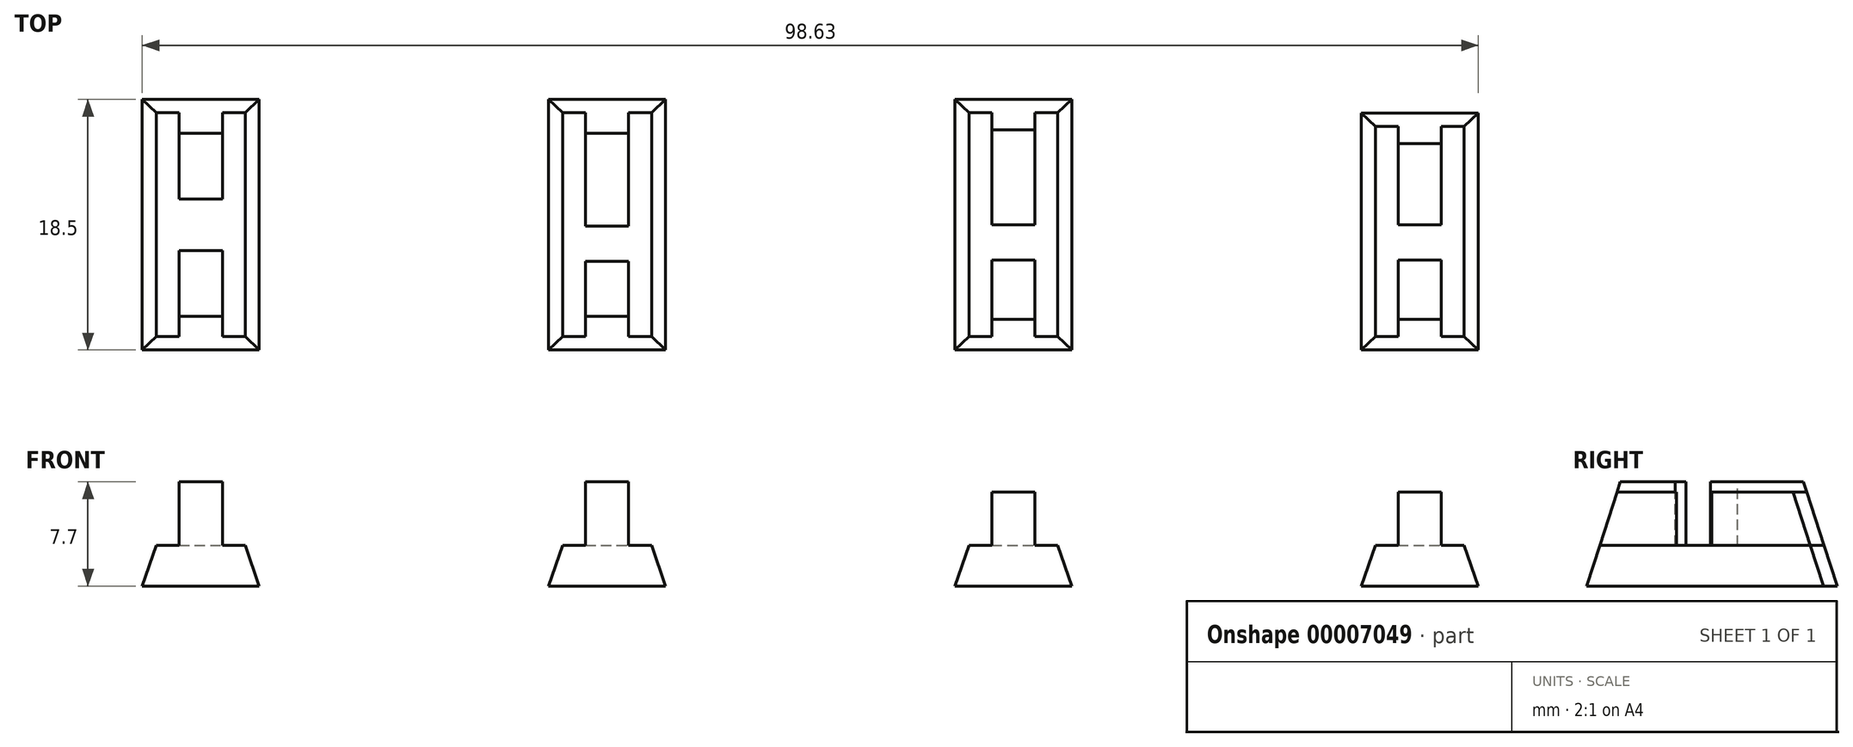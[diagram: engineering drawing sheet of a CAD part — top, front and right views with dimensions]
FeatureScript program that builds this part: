
annotation { "Feature Type Name" : "Feature", "Feature Type Description" : "" }
export const myFeature = defineFeature(function(context is Context, id is Id, definition is map)
    precondition{}
    {
        {
            var Q0;
            Q0=qCreatedBy(makeId("Front.planeOp"),FACE);
            var sketch = newSketch(context, id + "F0", { "sketchPlane" : qUnion([Q0])});
            skLineSegment(sketch, "E0", {"start": v(-34.23, 16.07) * mm, "end": v(-34.23, 12.67) * mm, "construction": true});
            skLineSegment(sketch, "E1", {"start": v(-34.23, 14.54) * mm, "end": v(-38.54, 14.54) * mm});
            skLineSegment(sketch, "E2", {"start": v(-38.54, 14.54) * mm, "end": v(-43.22, 14.54) * mm, "construction": true});
            skLineSegment(sketch, "E3", {"start": v(-43.22, 14.54) * mm, "end": v(-43.22, 17.54) * mm, "construction": true});
            skLineSegment(sketch, "E4", {"start": v(-43.22, 17.54) * mm, "end": v(-31.38, 17.54) * mm, "construction": true});
            skLineSegment(sketch, "E5", {"start": v(-37.5, 16.07) * mm, "end": v(-37.5, 22.5) * mm, "construction": true});
            skLineSegment(sketch, "E6", {"start": v(-38.54, 14.54) * mm, "end": v(-37.5, 17.54) * mm});
            skPoint(sketch, "E6.endSnap0", {"position": v(-37.3, 17.54) * mm});
            skLineSegment(sketch, "E7", {"start": v(-37.5, 17.54) * mm, "end": v(-35.82, 17.54) * mm});
            skLineSegment(sketch, "E8", {"start": v(-35.82, 17.54) * mm, "end": v(-35.82, 22.24) * mm});
            skLineSegment(sketch, "E9", {"start": v(-34.23, 14.54) * mm, "end": v(-34.23, 23.56) * mm, "construction": true});
            skLineSegment(sketch, "E10", {"start": v(-35.82, 22.24) * mm, "end": v(-34.23, 22.24) * mm});
            skLineSegment(sketch, "E11", {"start": v(-34.23, 22.24) * mm, "end": v(-34.23, 14.54) * mm});
            skSolve(sketch);
        }
        {
            var Q0;
            Q0=makeQuery(id+"F0.imprint","IMPRINT",FACE,{"disambiguationData":[TD([[makeQuery(id+"F0.imprint","IMPRINT",EDGE,{"derivedFrom":sQuery(id+"F0.wireOp",EDGE,"E1")}),-1.0]])]});
            extrude(context, id + "F1", {"entities" : qUnion([Q0]), "depth" : 18.5 * mm});
        }
        {
            var Q0;
            Q0=makeQuery(id+"F1.opExtrude","SWEPT_FACE",FACE,{"disambiguationData":[OSD([sQuery(id+"F0.wireOp",EDGE,"E11")])]});
            var sketch = newSketch(context, id + "F2", { "sketchPlane" : qUnion([Q0])});
            skLineSegment(sketch, "E12", {"start": v(-9.25, 22.24) * mm, "end": v(-9.25, 26.61) * mm, "construction": true});
            skCircle(sketch, "E13", {"center": v(-9.25, 26.61) * mm, "radius": 1.9 * mm, "construction": true});
            skLineSegment(sketch, "E14", {"start": v(-18.5, 14.54) * mm, "end": v(-16, 22.24) * mm});
            skLineSegment(sketch, "E15.MirrorCS", {"start": v(0, 14.54) * mm, "end": v(-2.5, 22.24) * mm});
            skLineSegment(sketch, "E16", {"start": v(-9.25, 26.61) * mm, "end": v(-11.15, 26.61) * mm, "construction": true});
            skLineSegment(sketch, "E17", {"start": v(-11.15, 26.61) * mm, "end": v(-11.15, 12.36) * mm, "construction": true});
            skLineSegment(sketch, "E18", {"start": v(-11.15, 22.24) * mm, "end": v(-11.15, 17.54) * mm});
            skLineSegment(sketch, "E19.MirrorCS", {"start": v(-7.35, 22.24) * mm, "end": v(-7.35, 17.54) * mm});
            skLineSegment(sketch, "E20", {"start": v(-11.15, 17.54) * mm, "end": v(-7.35, 17.54) * mm});
            skSolve(sketch);
        }
        {
            var Q0;
            {var subQ3=sQuery(id+"F2.wireOp",EDGE,"E14");Q0=makeQuery(id+"F2.imprint","IMPRINT",FACE,{"disambiguationData":[TD([[makeQuery(id+"F2.imprint","IMPRINT",EDGE,{"derivedFrom":subQ3}),1.0]])]});}
            var Q1;
            {var subQ3=sQuery(id+"F2.wireOp",EDGE,"E15.MirrorCS");Q1=makeQuery(id+"F2.imprint","IMPRINT",FACE,{"disambiguationData":[TD([[makeQuery(id+"F2.imprint","IMPRINT",EDGE,{"derivedFrom":subQ3}),-1.0]])]});}
            var Q2;
            {var subQ2=sQuery(id+"F2.wireOp",EDGE,"E18");Q2=makeQuery(id+"F2.imprint","IMPRINT",FACE,{"disambiguationData":[TD([[makeQuery(id+"F2.imprint","IMPRINT",EDGE,{"derivedFrom":subQ2}),1.0]])]});}
            extrude(context, id + "F3", {"entities" : qUnion([Q0, Q1, Q2]), "operationType" : NewBodyOperationType.REMOVE, "oppositeDirection" : true, "depth" : 10 * mm});
        }
        {
            var Q0;
            Q0=makeQuery(id+"F1.opExtrude","SWEPT_BODY",BODY,{"disambiguationData":[OSD([sQuery(id+"F0.wireOp",EDGE,"E1"),sQuery(id+"F0.wireOp",EDGE,"E6"),sQuery(id+"F0.wireOp",EDGE,"E7"),sQuery(id+"F0.wireOp",EDGE,"E8"),sQuery(id+"F0.wireOp",EDGE,"E10"),sQuery(id+"F0.wireOp",EDGE,"E11")])]});
            var Q1;
            Q1=makeQuery(id+"F1.opExtrude","SWEPT_FACE",FACE,{"disambiguationData":[OSD([sQuery(id+"F0.wireOp",EDGE,"E11")])]});
            mirror(context, id + "F4", {"operationType" : NewBodyOperationType.ADD, "entities" : qUnion([Q0]), "mirrorPlane" : qUnion([Q1])});
        }
        {
            var Q0;
            Q0=makeQuery(id+"F1.opExtrude","SWEPT_BODY",BODY,{"disambiguationData":[OSD([sQuery(id+"F0.wireOp",EDGE,"E1"),sQuery(id+"F0.wireOp",EDGE,"E6"),sQuery(id+"F0.wireOp",EDGE,"E7"),sQuery(id+"F0.wireOp",EDGE,"E8"),sQuery(id+"F0.wireOp",EDGE,"E10"),sQuery(id+"F0.wireOp",EDGE,"E11")])]});
            transform(context, id + "F5", {"entities" : qUnion([Q0]), "transformType" : TransformType.TRANSLATION_3D, "dx" : 30 * mm, "dy" : 0 * mm, "dz" : 0 * mm, "makeCopy" : true});
        }
        {
            var Q0;
            {var subQ0=makeQuery(id+"F3.boolean.opBoolean","COPY",FACE,{"derivedFrom":makeQuery(id+"F3.opExtrude","SWEPT_FACE",FACE,{"disambiguationData":[OSD([sQuery(id+"F2.wireOp",EDGE,"E19.MirrorCS")])]})});Q0=makeQuery(id+"F5.opPattern","COPY",FACE,{"derivedFrom":makeQuery(id+"F4.boolean.opBoolean","MERGE",FACE,{"derivedFrom":[subQ0,makeQuery(id+"F4.opPattern","COPY",FACE,{"derivedFrom":subQ0,"instanceName":"1"})]}),"instanceName":"1"});}
            extrude(context, id + "F6", {"entities" : qUnion([Q0]), "operationType" : NewBodyOperationType.ADD, "depth" : 2 * mm});
        }
        {
            var Q0;
            {var subQ0=makeQuery(id+"F3.boolean.opBoolean","COPY",FACE,{"derivedFrom":makeQuery(id+"F3.opExtrude","SWEPT_FACE",FACE,{"disambiguationData":[OSD([sQuery(id+"F2.wireOp",EDGE,"E18")])]})});Q0=makeQuery(id+"F5.opPattern","COPY",FACE,{"derivedFrom":makeQuery(id+"F4.boolean.opBoolean","MERGE",FACE,{"derivedFrom":[subQ0,makeQuery(id+"F4.opPattern","COPY",FACE,{"derivedFrom":subQ0,"instanceName":"1"})]}),"instanceName":"1"});}
            extrude(context, id + "F7", {"entities" : qUnion([Q0]), "operationType" : NewBodyOperationType.REMOVE, "oppositeDirection" : true, "depth" : 0.8 * mm});
        }
        {
            var Q0;
            Q0=makeQuery(id+"F5.opPattern","COPY",BODY,{"derivedFrom":makeQuery(id+"F1.opExtrude","SWEPT_BODY",BODY,{"disambiguationData":[OSD([sQuery(id+"F0.wireOp",EDGE,"E1"),sQuery(id+"F0.wireOp",EDGE,"E6"),sQuery(id+"F0.wireOp",EDGE,"E7"),sQuery(id+"F0.wireOp",EDGE,"E8"),sQuery(id+"F0.wireOp",EDGE,"E10"),sQuery(id+"F0.wireOp",EDGE,"E11")])]}),"instanceName":"1"});
            transform(context, id + "F8", {"entities" : qUnion([Q0]), "transformType" : TransformType.TRANSLATION_3D, "dx" : 30 * mm, "dy" : 0 * mm, "dz" : 0 * mm, "makeCopy" : true});
        }
        {
            var Q0;
            Q0=makeQuery(id+"F8.opPattern","COPY",FACE,{"derivedFrom":makeQuery(id+"F6.opExtrude","CAP_FACE",FACE,{"disambiguationData":[OSD([sQuery(id+"F2.wireOp",EDGE,"E19.MirrorCS")])],"isStart":false}),"instanceName":"1"});
            extrude(context, id + "F9", {"entities" : qUnion([Q0]), "operationType" : NewBodyOperationType.REMOVE, "oppositeDirection" : true, "depth" : 0.1 * mm});
        }
        {
            var Q0;
            Q0=makeQuery(id+"F8.opPattern","COPY",FACE,{"derivedFrom":makeQuery(id+"F7.boolean.opBoolean","COPY",FACE,{"derivedFrom":makeQuery(id+"F7.opExtrude","CAP_FACE",FACE,{"disambiguationData":[OSD([sQuery(id+"F2.wireOp",EDGE,"E18")])],"isStart":false})}),"instanceName":"1"});
            extrude(context, id + "F10", {"entities" : qUnion([Q0]), "operationType" : NewBodyOperationType.ADD, "depth" : 0.1 * mm});
        }
        {
            var Q0;
            {var subQ0=sQuery(id+"F0.wireOp",EDGE,"E10");var subQ1=sQuery(id+"F0.wireOp",EDGE,"E11");var subQ2=sQuery(id+"F2.wireOp",EDGE,"E18");var subQ3=makeQuery(id+"F3.boolean.opBoolean","SPLIT",FACE,{"disambiguationData":[TD([makeQuery(id+"F3.opExtrude","SWEPT_FACE",FACE,{"disambiguationData":[OSD([sQuery(id+"F2.wireOp",EDGE,"E14")])]})])],"derivedFrom":makeQuery(id+"F1.opExtrude","SWEPT_FACE",FACE,{"disambiguationData":[OSD([subQ0])]})});Q0=makeQuery(id+"F10.boolean.opBoolean","MERGE",FACE,{"derivedFrom":[makeQuery(id+"F8.opPattern","COPY",FACE,{"derivedFrom":makeQuery(id+"F5.opPattern","COPY",FACE,{"derivedFrom":makeQuery(id+"F4.boolean.opBoolean","MERGE",FACE,{"derivedFrom":[subQ3,makeQuery(id+"F4.opPattern","COPY",FACE,{"derivedFrom":subQ3,"instanceName":"1"})]}),"instanceName":"1"}),"instanceName":"1"}),makeQuery(id+"F10.opExtrude","SWEPT_FACE",FACE,{"disambiguationData":[OSD([subQ0,subQ1,subQ2])]})]});}
            var Q1;
            {var subQ0=sQuery(id+"F0.wireOp",EDGE,"E10");var subQ1=sQuery(id+"F2.wireOp",EDGE,"E19.MirrorCS");var subQ2=sQuery(id+"F0.wireOp",EDGE,"E11");var subQ3=makeQuery(id+"F3.boolean.opBoolean","SPLIT",FACE,{"disambiguationData":[TD([makeQuery(id+"F3.opExtrude","SWEPT_FACE",FACE,{"disambiguationData":[OSD([sQuery(id+"F2.wireOp",EDGE,"E15.MirrorCS")])]})])],"derivedFrom":makeQuery(id+"F1.opExtrude","SWEPT_FACE",FACE,{"disambiguationData":[OSD([subQ0])]})});Q1=makeQuery(id+"F8.opPattern","COPY",FACE,{"derivedFrom":makeQuery(id+"F6.boolean.opBoolean","MERGE",FACE,{"derivedFrom":[makeQuery(id+"F5.opPattern","COPY",FACE,{"derivedFrom":makeQuery(id+"F4.boolean.opBoolean","MERGE",FACE,{"derivedFrom":[subQ3,makeQuery(id+"F4.opPattern","COPY",FACE,{"derivedFrom":subQ3,"instanceName":"1"})]}),"instanceName":"1"}),makeQuery(id+"F6.opExtrude","SWEPT_FACE",FACE,{"disambiguationData":[OSD([subQ0,subQ2,subQ1])]})]}),"instanceName":"1"});}
            extrude(context, id + "F11", {"entities" : qUnion([Q0, Q1]), "operationType" : NewBodyOperationType.REMOVE, "oppositeDirection" : true, "depth" : 0.75 * mm});
        }
        {
            var Q0;
            Q0=makeQuery(id+"F11.boolean.opBoolean","COPY",FACE,{"derivedFrom":makeQuery(id+"F11.opExtrude","SWEPT_FACE",FACE,{"disambiguationData":[OSD([sQuery(id+"F0.wireOp",EDGE,"E10"),sQuery(id+"F0.wireOp",EDGE,"E11"),sQuery(id+"F2.wireOp",EDGE,"E14")])]})});
            extrude(context, id + "F12", {"entities" : qUnion([Q0]), "operationType" : NewBodyOperationType.REMOVE, "oppositeDirection" : true, "depth" : 2 * mm});
        }
        {
            var Q0;
            Q0=makeQuery(id+"F11.boolean.opBoolean","COPY",FACE,{"derivedFrom":makeQuery(id+"F11.opExtrude","SWEPT_FACE",FACE,{"disambiguationData":[OSD([sQuery(id+"F0.wireOp",EDGE,"E10"),sQuery(id+"F0.wireOp",EDGE,"E11"),sQuery(id+"F2.wireOp",EDGE,"E15.MirrorCS")])]})});
            extrude(context, id + "F13", {"entities" : qUnion([Q0]), "operationType" : NewBodyOperationType.REMOVE, "oppositeDirection" : true, "depth" : 2 * mm});
        }
        {
            var Q0;
            Q0=makeQuery(id+"F8.opPattern","COPY",BODY,{"derivedFrom":makeQuery(id+"F5.opPattern","COPY",BODY,{"derivedFrom":makeQuery(id+"F1.opExtrude","SWEPT_BODY",BODY,{"disambiguationData":[OSD([sQuery(id+"F0.wireOp",EDGE,"E1"),sQuery(id+"F0.wireOp",EDGE,"E6"),sQuery(id+"F0.wireOp",EDGE,"E7"),sQuery(id+"F0.wireOp",EDGE,"E8"),sQuery(id+"F0.wireOp",EDGE,"E10"),sQuery(id+"F0.wireOp",EDGE,"E11")])]}),"instanceName":"1"}),"instanceName":"1"});
            transform(context, id + "F14", {"entities" : qUnion([Q0]), "transformType" : TransformType.TRANSLATION_3D, "dx" : 30 * mm, "dy" : 0 * mm, "dz" : 0 * mm, "makeCopy" : true});
        }
        {
            var Q0;
            Q0=makeQuery(id+"F14.opPattern","COPY",FACE,{"derivedFrom":makeQuery(id+"F8.opPattern","COPY",FACE,{"derivedFrom":makeQuery(id+"F5.opPattern","COPY",FACE,{"derivedFrom":makeQuery(id+"F4.opPattern","COPY",FACE,{"derivedFrom":makeQuery(id+"F1.opExtrude","SWEPT_FACE",FACE,{"disambiguationData":[OSD([sQuery(id+"F0.wireOp",EDGE,"E6")])]}),"instanceName":"1"}),"instanceName":"1"}),"instanceName":"1"}),"instanceName":"1"});
            var sketch = newSketch(context, id + "F15", { "sketchPlane" : qUnion([Q0])});
            skLineSegment(sketch, "E21", {"start": v(0, -5.85) * mm, "end": v(-1, -5.85) * mm});
            skSolve(sketch);
        }
        {
            var Q0;
            {var subQ0=makeQuery(id+"F3.boolean.opBoolean","COPY",FACE,{"derivedFrom":makeQuery(id+"F3.opExtrude","SWEPT_FACE",FACE,{"disambiguationData":[OSD([sQuery(id+"F2.wireOp",EDGE,"E15.MirrorCS")])]})});Q0=makeQuery(id+"F14.opPattern","COPY",FACE,{"derivedFrom":makeQuery(id+"F8.opPattern","COPY",FACE,{"derivedFrom":makeQuery(id+"F5.opPattern","COPY",FACE,{"derivedFrom":makeQuery(id+"F4.boolean.opBoolean","MERGE",FACE,{"derivedFrom":[subQ0,makeQuery(id+"F4.opPattern","COPY",FACE,{"derivedFrom":subQ0,"instanceName":"1"})]}),"instanceName":"1"}),"instanceName":"1"}),"instanceName":"1"});}
            var Q1;
            Q1=sQuery(id+"F15.wireOp",EDGE,"E21");
            sweep(context, id + "F16", {"operationType" : NewBodyOperationType.REMOVE, "profiles" : qUnion([Q0]), "path" : qUnion([Q1])});
        }
    });
